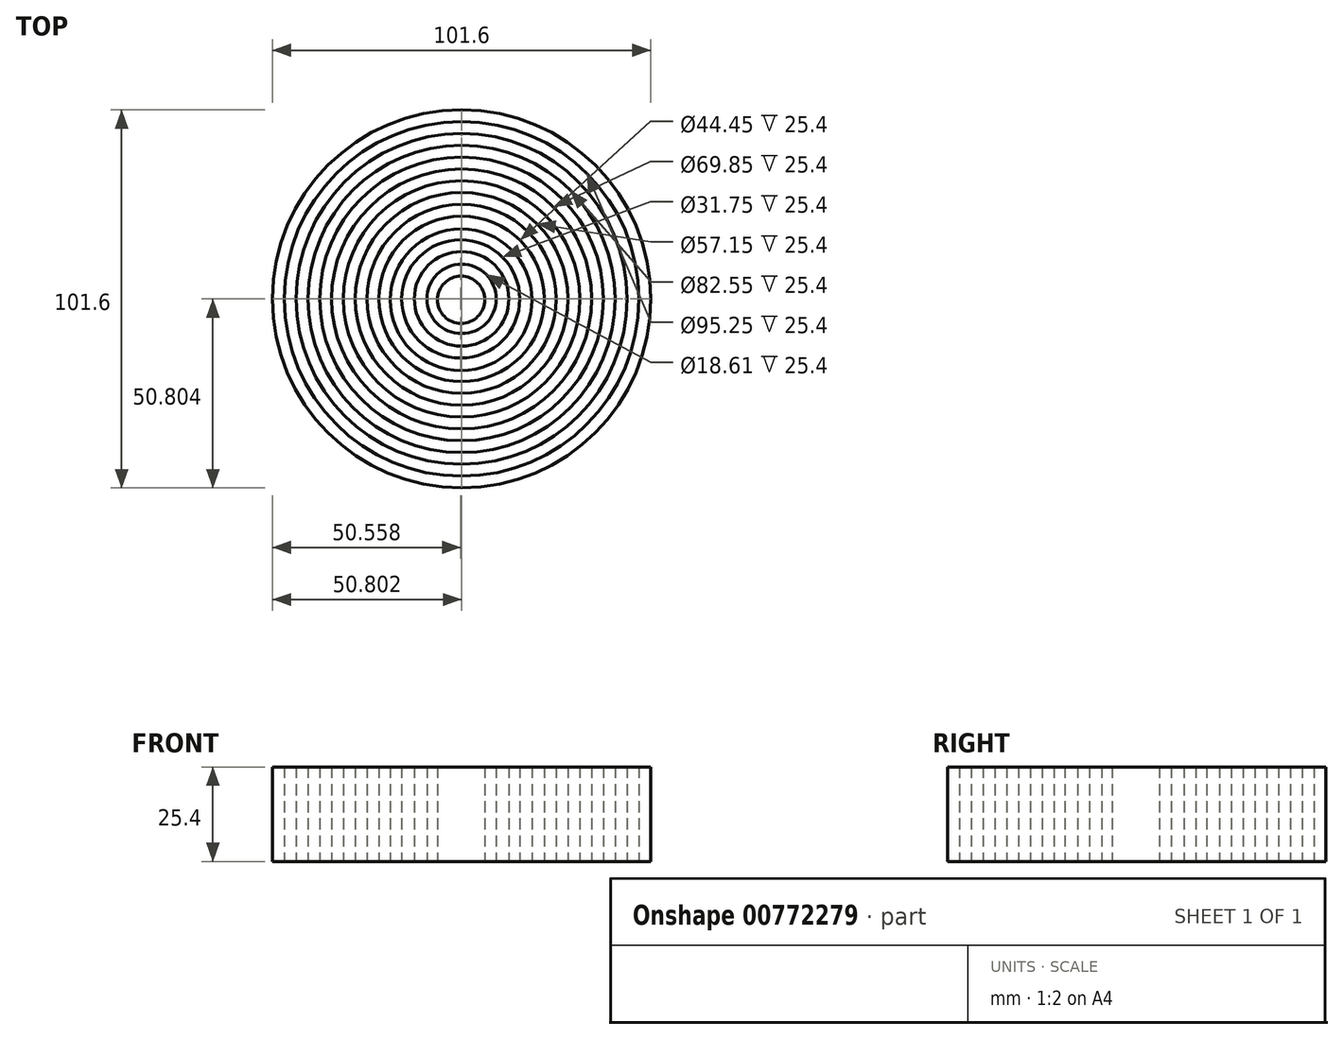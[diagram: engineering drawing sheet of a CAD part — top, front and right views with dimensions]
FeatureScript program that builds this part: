
annotation { "Feature Type Name" : "Feature", "Feature Type Description" : "" }
export const myFeature = defineFeature(function(context is Context, id is Id, definition is map)
    precondition{}
    {
        {
            var Q0;
            Q0=qCreatedBy(makeId("Top.planeOp"),FACE);
            var sketch = newSketch(context, id + "F0", { "sketchPlane" : qUnion([Q0])});
            skCircle(sketch, "E0", {"center": v(0, 0) * mm, "radius": 19.05 * mm});
            skCircle(sketch, "E1", {"center": v(0, 0) * mm, "radius": 6.35 * mm});
            skCircle(sketch, "E2", {"center": v(-0.12, 0.24) * mm, "radius": 15.88 * mm});
            skCircle(sketch, "E3", {"center": v(0.12, 0.24) * mm, "radius": 12.7 * mm});
            skCircle(sketch, "E4", {"center": v(0.12, 0.24) * mm, "radius": 25.4 * mm});
            skCircle(sketch, "E5", {"center": v(0.12, 0.24) * mm, "radius": 31.75 * mm});
            skCircle(sketch, "E6", {"center": v(0.12, 0.24) * mm, "radius": 34.93 * mm});
            skCircle(sketch, "E7", {"center": v(0.12, 0.24) * mm, "radius": 22.23 * mm});
            skCircle(sketch, "E8", {"center": v(0.12, 0.24) * mm, "radius": 28.58 * mm});
            skCircle(sketch, "E9", {"center": v(0.12, 0.24) * mm, "radius": 9.3 * mm});
            skCircle(sketch, "E10", {"center": v(0.12, 0.24) * mm, "radius": 38.1 * mm});
            skCircle(sketch, "E11", {"center": v(0.12, 0.24) * mm, "radius": 41.28 * mm});
            skCircle(sketch, "E12", {"center": v(0.12, 0.24) * mm, "radius": 44.45 * mm});
            skCircle(sketch, "E13", {"center": v(0.12, 0.24) * mm, "radius": 47.63 * mm});
            skCircle(sketch, "E14", {"center": v(0.12, 0.24) * mm, "radius": 50.8 * mm});
            skCircle(sketch, "E15", {"center": v(-0.12, 0.24) * mm, "radius": 53.98 * mm});
            skSolve(sketch);
        }
        {
            var Q0;
            Q0=makeQuery(id+"F0.imprint","IMPRINT",FACE,{"disambiguationData":[TD([[makeQuery(id+"F0.imprint","IMPRINT",EDGE,{"derivedFrom":sQuery(id+"F0.wireOp",EDGE,"E1")}),1.0]])]});
            var Q1;
            Q1=makeQuery(id+"F0.imprint","IMPRINT",FACE,{"disambiguationData":[TD([[makeQuery(id+"F0.imprint","IMPRINT",EDGE,{"derivedFrom":sQuery(id+"F0.wireOp",EDGE,"E3")}),1.0]])]});
            var Q2;
            Q2=makeQuery(id+"F0.imprint","IMPRINT",FACE,{"disambiguationData":[TD([[makeQuery(id+"F0.imprint","IMPRINT",EDGE,{"derivedFrom":sQuery(id+"F0.wireOp",EDGE,"E0")}),1.0]])]});
            var Q3;
            Q3=makeQuery(id+"F0.imprint","IMPRINT",FACE,{"disambiguationData":[TD([[makeQuery(id+"F0.imprint","IMPRINT",EDGE,{"derivedFrom":sQuery(id+"F0.wireOp",EDGE,"E4")}),1.0]])]});
            var Q4;
            Q4=makeQuery(id+"F0.imprint","IMPRINT",FACE,{"disambiguationData":[TD([[makeQuery(id+"F0.imprint","IMPRINT",EDGE,{"derivedFrom":sQuery(id+"F0.wireOp",EDGE,"E5")}),1.0]])]});
            extrude(context, id + "F1", {"entities" : qUnion([Q0, Q1, Q2, Q3, Q4]), "depth" : 25.4 * mm, "offsetDistance" : 25.4 * mm});
        }
        {
            var Q0;
            Q0=makeQuery(id+"F0.imprint","IMPRINT",FACE,{"disambiguationData":[TD([[makeQuery(id+"F0.imprint","IMPRINT",EDGE,{"derivedFrom":sQuery(id+"F0.wireOp",EDGE,"E6")}),-1.0]])]});
            var Q1;
            Q1=makeQuery(id+"F0.imprint","IMPRINT",FACE,{"disambiguationData":[TD([[makeQuery(id+"F0.imprint","IMPRINT",EDGE,{"derivedFrom":sQuery(id+"F0.wireOp",EDGE,"E11")}),-1.0]])]});
            var Q2;
            Q2=makeQuery(id+"F0.imprint","IMPRINT",FACE,{"disambiguationData":[TD([[makeQuery(id+"F0.imprint","IMPRINT",EDGE,{"derivedFrom":sQuery(id+"F0.wireOp",EDGE,"E13")}),-1.0]])]});
            extrude(context, id + "F2", {"entities" : qUnion([Q0, Q1, Q2]), "depth" : 25.4 * mm, "offsetDistance" : 25.4 * mm});
        }
    });
